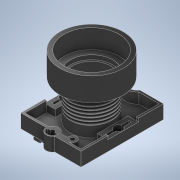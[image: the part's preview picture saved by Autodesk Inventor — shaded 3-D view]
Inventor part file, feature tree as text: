
AUTODESK INVENTOR PART (.ipt)
format: ipt  version: 2022 (Build 260153000, 153)  size: 650,752 bytes
history: native  units: mm
features: extrude x15, sketch x9, plane x4, emboss x4, other x3, projected_geometry x2, thread x1
ambient origin geometry x8: Origin, YZ Plane, XZ Plane, XY Plane, X Axis, Y Axis, Z Axis, Center Point
bodies: Solid1 (feature_tree)
feature tree (38):
  extrude  "Extrusion1"  Depth=40.0mm
  sketch  "Sketch2"  dims[d2=6.5mm d3=0.0mm d4=18.0mm]
  extrude  "Extrusion2"  Depth=6.5mm
  extrude  "Extrusion3"  TaperAngle=0.0deg  [1 undecoded]
  extrude  "Extrusion4"  Depth=11.0mm
  extrude  "Extrusion5"  Depth=0.6mm
  extrude  "Extrusion6"  Depth=5.5mm
  sketch  "Sketch4"  dims[d5=0.0mm d6=0.0mm]
  extrude  "Extrusion7"  Depth=2.0mm
  extrude  "Extrusion8"  Depth=3.592122mm
  plane  "Work Plane2"
  plane  "Work Plane1"
  plane  "Work Plane3"
  thread  "Thread1"  [1 undecoded]
  extrude  "Extrusion13"  Depth=2.0mm
  sketch  "Sketch11"  dims[d10=5.5mm d11=0.6mm]
  extrude  "Extrusion14"  Depth=1.5mm
  extrude  "Extrusion15"  Depth=1.5mm
  extrude  "Extrusion16"  Depth=1.5mm
  extrude  "Extrusion17"  Depth=1.5mm
  sketch  "Sketch12"  dims[d12=0.6mm d13=5.5mm]
  sketch  "Sketch13"  dims[d14=5.5mm d15=2.0mm]
  emboss  "Emboss1"
  emboss  "Emboss2"
  emboss  "Emboss3"
  emboss  "Emboss4"
  other  "Work Axis1"
  other  "Work Axis2"
  other  "Work Axis3"
  extrude  "Extrusion18"  Depth=1.0mm
  plane  "Work Plane4"
  extrude  "Extrusion19"  Depth=2.0mm
  sketch  "Sketch1"  dims[d0=30.0mm d1=40.0mm]
  projected_geometry  "Projected Loop2"
  sketch  "Sketch6"  dims[d7=4.0mm d8=2.3mm d9=11.0mm]
  projected_geometry  "Projected Loop3"
  sketch  "Sketch14"  dims[d16=1.2mm d17=3.592122mm d18=1.2mm]
  sketch  "Sketch15"  dims[d19=3.592122mm d20=2.0mm d21=1.5mm d22=1.5mm d24=1.5mm d25=1.5mm d29=1.0mm d30=2.0mm d31=7.0mm d32=3.0mm d33=2.0mm d34=7.0mm d35=3.0mm d36=6.0mm d37=1.5mm d38=3.0mm d39=0.5mm d40=2.0mm d41=1.0mm d42=19.0mm d43=4.0mm d44=6.5mm d45=0.0mm d46=0.5mm d47=0.0mm d48=0.5mm d49=0.0mm d50=7.25mm d51=7.25mm d52=5.0mm d53=1.0mm d54=0.0mm d55=1.6mm d56=0.0mm d57=1.0mm d60=20.0mm d61=13.0mm d62=0.0mm d63=30.0mm d64=2.0mm d65=0.0mm d82=0.25mm d83=0.25mm d85=0.25mm d86=0.25mm d87=0.25mm d88=0.5mm d91=8.5mm d92=0.0mm d93=5.0mm d94=0.0mm d98=3.0mm d99=2.0mm d100=3.0mm d101=2.0mm d102=0.5mm d103=0.0mm d104=1.5mm d105=0.0mm d106=3.0mm d107=2.0mm d108=3.0mm d109=2.0mm d110=0.5mm d111=0.0mm d112=1.5mm d113=0.0mm d114=0.1mm d115=0.0mm d116=0.1mm d117=0.0mm d118=0.1mm d119=0.0mm d120=0.1mm d121=0.0mm d122=1.5mm d123=1.5mm d124=1.7mm d125=1.4mm d126=1.7mm d127=1.4mm d128=0.75mm d129=6.25mm d130=0.75mm d131=5.5mm d132=5.5mm d136=1.5mm d137=1.2mm d138=2.3mm d139=2.0mm d140=2.0mm d141=1.2mm d142=11.0mm d143=1.5mm d144=1.7mm d145=1.7mm d146=1.4mm d147=6.25mm d148=6.25mm d149=7.25mm d150=7.25mm d151=6.25mm d152=2.0mm d153=9.0mm d154=0.0mm d155=-7.0mm d156=2.0mm d157=2.0mm d158=2.0mm d159=1.0mm d160=0.0mm]
note: 2 required parameter values undecoded (feature->parameter linkage not recoverable at this tier; creation-order binding heuristic only, values carry confidence <= 0.55)
